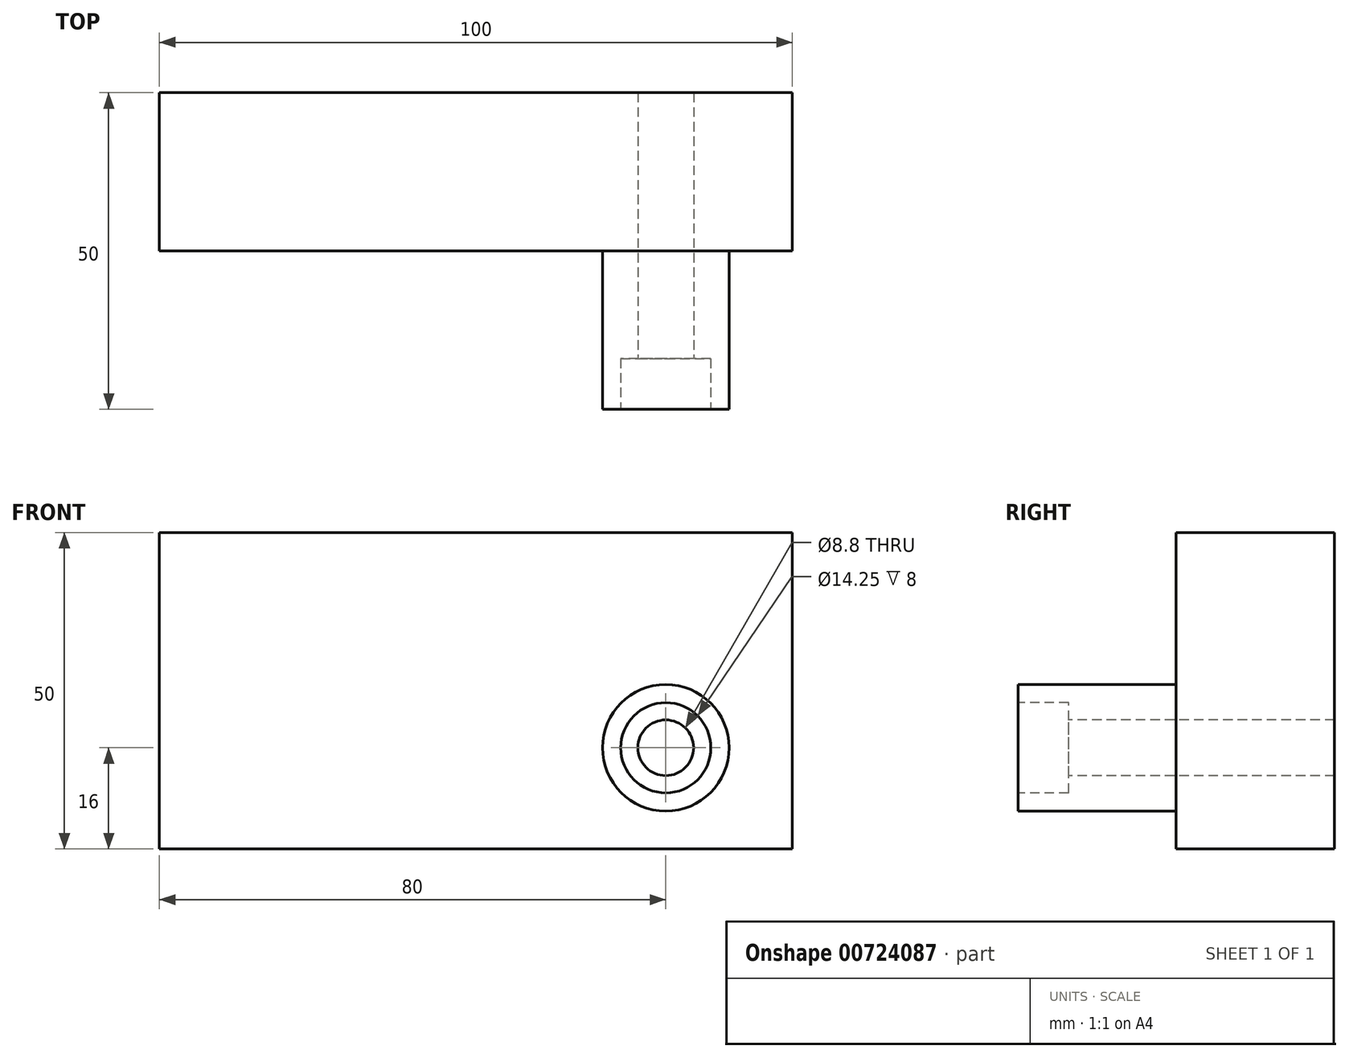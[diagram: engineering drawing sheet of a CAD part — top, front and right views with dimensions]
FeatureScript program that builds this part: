
annotation { "Feature Type Name" : "Feature", "Feature Type Description" : "" }
export const myFeature = defineFeature(function(context is Context, id is Id, definition is map)
    precondition{}
    {
        {
            var Q0;
            Q0=qCreatedBy(makeId("Front.planeOp"),FACE);
            var sketch = newSketch(context, id + "F0", { "sketchPlane" : qUnion([Q0])});
            skLineSegment(sketch, "E0.bottom", {"start": v(0, 0) * mm, "end": v(100, 0) * mm});
            skLineSegment(sketch, "E0.top", {"start": v(0, -50) * mm, "end": v(100, -50) * mm});
            skLineSegment(sketch, "E0.left", {"start": v(0, 0) * mm, "end": v(0, -50) * mm});
            skLineSegment(sketch, "E0.right", {"start": v(100, 0) * mm, "end": v(100, -50) * mm});
            skSolve(sketch);
        }
        {
            var Q0;
            Q0=makeQuery(id+"F0.imprint","IMPRINT",FACE,{"disambiguationData":[TD([[makeQuery(id+"F0.imprint","IMPRINT",EDGE,{"derivedFrom":sQuery(id+"F0.wireOp",EDGE,"E0.bottom")}),-1.0]])]});
            extrude(context, id + "F1", {"entities" : qUnion([Q0]), "depth" : 25 * mm, "offsetDistance" : 25 * mm});
        }
        {
            var Q0;
            Q0=makeQuery(id+"F1.opExtrude","CAP_FACE",FACE,{"disambiguationData":[OSD([sQuery(id+"F0.wireOp",EDGE,"E0.bottom"),sQuery(id+"F0.wireOp",EDGE,"E0.top"),sQuery(id+"F0.wireOp",EDGE,"E0.left"),sQuery(id+"F0.wireOp",EDGE,"E0.right")])],"isStart":false});
            var sketch = newSketch(context, id + "F2", { "sketchPlane" : qUnion([Q0])});
            skCircle(sketch, "E1", {"center": v(80, -34) * mm, "radius": 10 * mm});
            skSolve(sketch);
        }
        {
            var Q0;
            Q0 = qSketchRegion(id + "F2", true);
            extrude(context, id + "F3", {"entities" : qUnion([Q0]), "operationType" : NewBodyOperationType.ADD, "depth" : 25 * mm, "offsetDistance" : 25 * mm});
        }
        {
            var Q0;
            Q0=makeQuery(id+"F3.opExtrude","CAP_FACE",FACE,{"disambiguationData":[OSD([sQuery(id+"F2.wireOp",EDGE,"E1")])],"isStart":false});
            var sketch = newSketch(context, id + "F4", { "sketchPlane" : qUnion([Q0])});
            skPoint(sketch, "E2", {"position": v(80, -34) * mm});
            skSolve(sketch);
        }
        {
            var Q0;
            Q0=sQuery(id+"F4.wireOp",VERTEX,"E2");
            var Q1;
            Q1=makeQuery(id+"F1.opExtrude","SWEPT_BODY",BODY,{"disambiguationData":[OSD([sQuery(id+"F0.wireOp",EDGE,"E0.bottom"),sQuery(id+"F0.wireOp",EDGE,"E0.top"),sQuery(id+"F0.wireOp",EDGE,"E0.left"),sQuery(id+"F0.wireOp",EDGE,"E0.right")])]});
            hole(context, id + "F5", {"style" : HoleStyle.C_BORE, "endStyle" : HoleEndStyle.THROUGH, "standardTappedOrClearance" : lookupTablePath({ "standard" : "ISO", "fit" : "Normal", "size" : "M8", "type" : "Clearance" }), "standardBlindInLast" : lookupTablePath({ "fit" : "Standard", "standard" : "ISO", "size" : "M8", "type" : "Clearance" }), "holeDiameter" : 8.8 * mm, "cBoreDiameter" : 14.25 * mm, "cBoreDepth" : 8 * mm, "majorDiameter" : 5 * mm, "isTappedThrough" : true, "tappedDepth" : 12 * mm, "tapClearance" : 3, "startFromSketch" : true, "locations" : qUnion([Q0]), "scope" : qUnion([Q1])});
        }
    });
